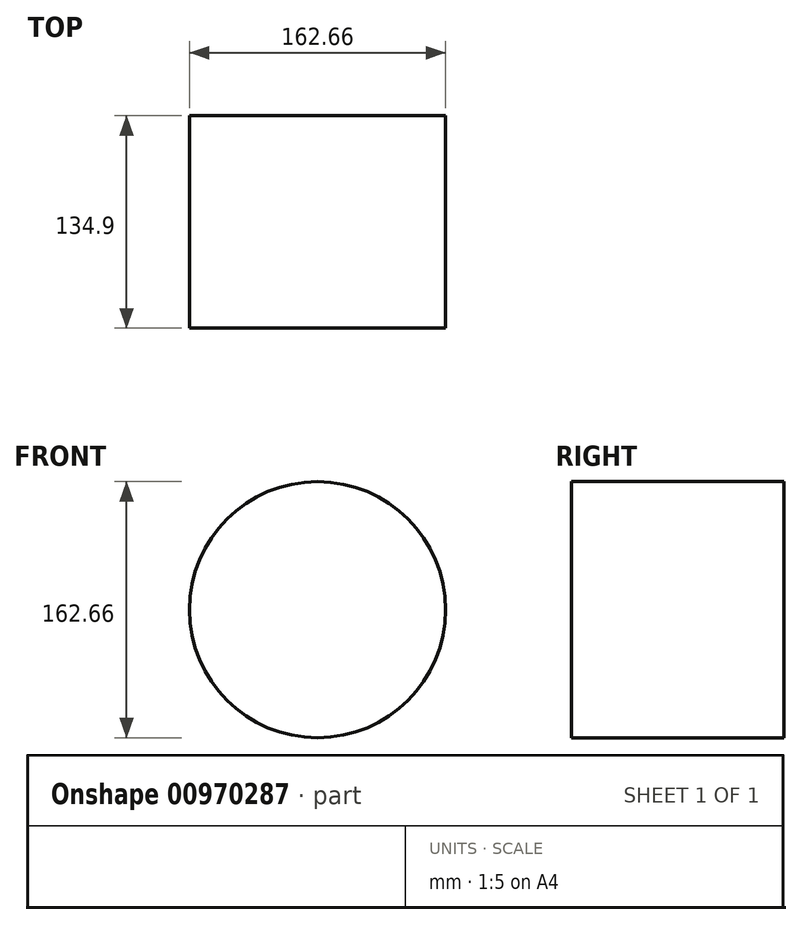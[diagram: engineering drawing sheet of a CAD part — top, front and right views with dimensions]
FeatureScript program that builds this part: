
annotation { "Feature Type Name" : "Feature", "Feature Type Description" : "" }
export const myFeature = defineFeature(function(context is Context, id is Id, definition is map)
    precondition{}
    {
        {
            var Q0;
            Q0=qCreatedBy(makeId("Right.planeOp"),FACE);
            var sketch = newSketch(context, id + "F0", { "sketchPlane" : qUnion([Q0])});
            skLineSegment(sketch, "E0.bottom", {"start": v(0, 0) * mm, "end": v(-134.9, 0) * mm});
            skLineSegment(sketch, "E0.top", {"start": v(0, -81.33) * mm, "end": v(-134.9, -81.33) * mm});
            skLineSegment(sketch, "E0.left", {"start": v(0, 0) * mm, "end": v(0, -81.33) * mm});
            skLineSegment(sketch, "E0.right", {"start": v(-134.9, 0) * mm, "end": v(-134.9, -81.33) * mm});
            skSolve(sketch);
        }
        {
            var Q0;
            Q0=makeQuery(id+"F0.imprint","IMPRINT",FACE,{"disambiguationData":[TD([[makeQuery(id+"F0.imprint","IMPRINT",EDGE,{"derivedFrom":sQuery(id+"F0.wireOp",EDGE,"E0.bottom")}),1.0]])]});
            var Q1;
            Q1=sQuery(id+"F0.wireOp",EDGE,"E0.bottom");
            revolve(context, id + "F1", {"surfaceOperationType" : NewSurfaceOperationType.NEW, "entities" : qUnion([Q0]), "axis" : qUnion([Q1]), "revolveType" : RevolveType.FULL});
        }
    });
